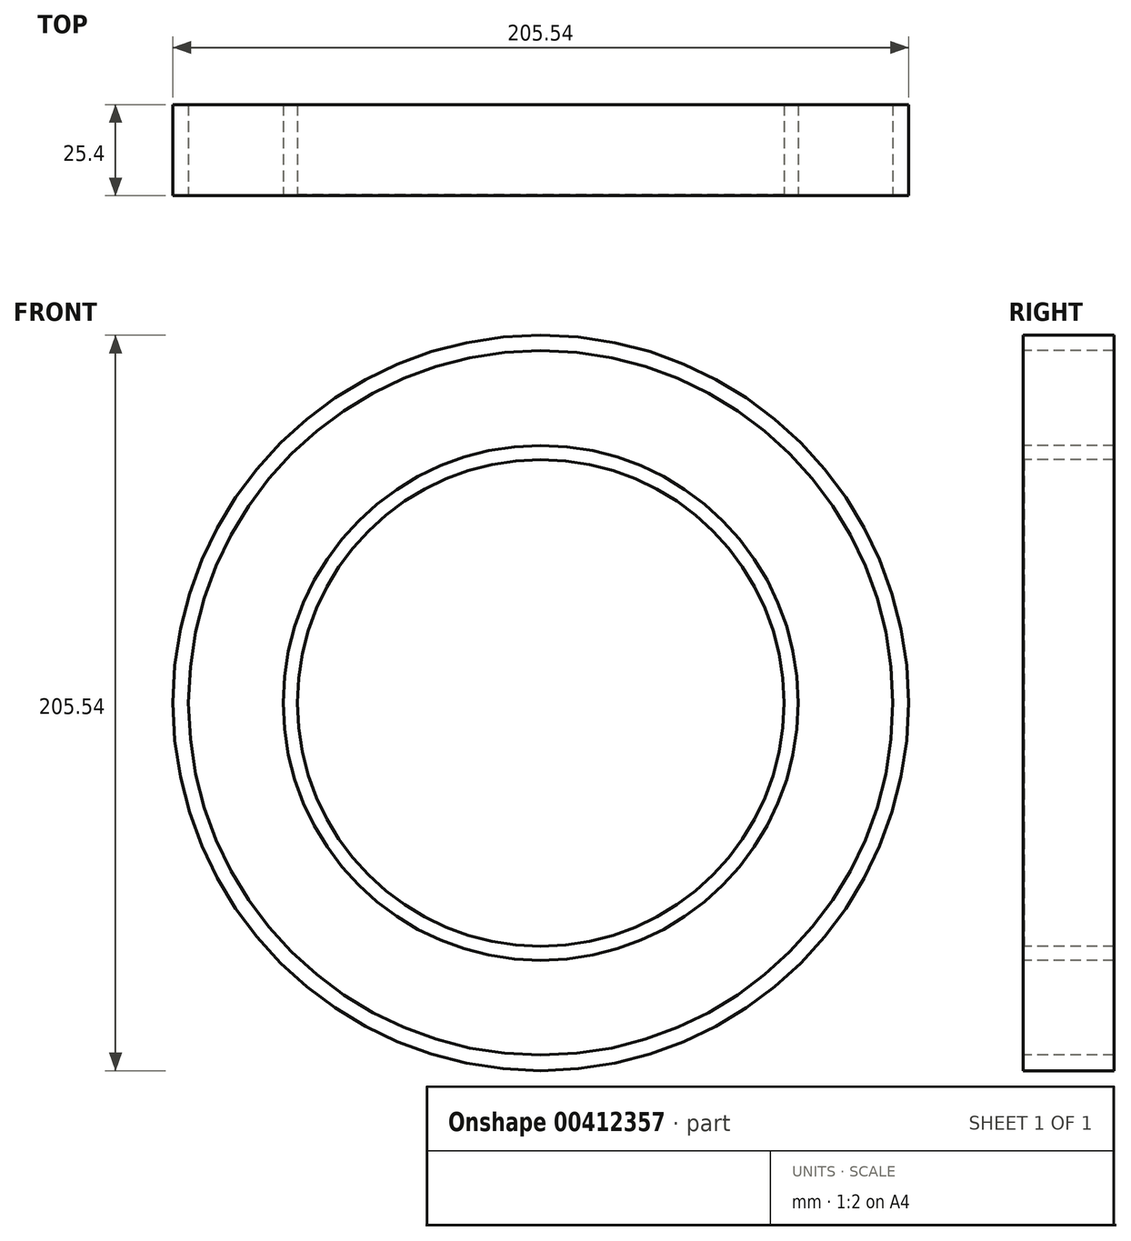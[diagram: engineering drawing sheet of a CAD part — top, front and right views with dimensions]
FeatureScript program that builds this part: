
annotation { "Feature Type Name" : "Feature", "Feature Type Description" : "" }
export const myFeature = defineFeature(function(context is Context, id is Id, definition is map)
    precondition{}
    {
        {
            var Q0;
            Q0=qCreatedBy(makeId("Front.planeOp"),FACE);
            var sketch = newSketch(context, id + "F0", { "sketchPlane" : qUnion([Q0])});
            skCircle(sketch, "E0", {"center": v(0, 0) * mm, "radius": 96.73 * mm});
            skCircle(sketch, "E1", {"center": v(0, 0) * mm, "radius": 101.89 * mm});
            skCircle(sketch, "E2", {"center": v(0, 0) * mm, "radius": 73.38 * mm});
            skCircle(sketch, "E3", {"center": v(0, 0) * mm, "radius": 68 * mm});
            skSolve(sketch);
        }
        {
            var Q0;
            Q0=makeQuery(id+"F0.imprint","IMPRINT",FACE,{"disambiguationData":[TD([[makeQuery(id+"F0.imprint","IMPRINT",EDGE,{"derivedFrom":sQuery(id+"F0.wireOp",EDGE,"E3")}),1.0]])]});
            var Q1;
            Q1=sQuery(id+"F0.wireOp",EDGE,"E3");
            extrude(context, id + "F1", {"entities" : qUnion([Q0]), "bodyType" : ToolBodyType.SURFACE, "surfaceEntities" : qUnion([Q1]), "depth" : 25.13 * mm});
        }
        {
            var Q0;
            Q0=qCreatedBy(makeId("Front.planeOp"),FACE);
            var sketch = newSketch(context, id + "F2", { "sketchPlane" : qUnion([Q0])});
            skCircle(sketch, "E4", {"center": v(0, 0) * mm, "radius": 71.95 * mm});
            skSolve(sketch);
        }
        {
            var Q0;
            Q0=makeQuery(id+"F2.imprint","IMPRINT",FACE,{"disambiguationData":[TD([[makeQuery(id+"F2.imprint","IMPRINT",EDGE,{"derivedFrom":sQuery(id+"F2.wireOp",EDGE,"E4")}),1.0]])]});
            var Q1;
            Q1=sQuery(id+"F2.wireOp",EDGE,"E4");
            extrude(context, id + "F3", {"entities" : qUnion([Q0]), "bodyType" : ToolBodyType.SURFACE, "surfaceEntities" : qUnion([Q1]), "depth" : 25.4 * mm});
        }
        {
            var Q0;
            Q0=qCreatedBy(makeId("Front.planeOp"),FACE);
            var sketch = newSketch(context, id + "F4", { "sketchPlane" : qUnion([Q0])});
            skCircle(sketch, "E5", {"center": v(0, 0) * mm, "radius": 98.42 * mm});
            skSolve(sketch);
        }
        {
            var Q0;
            Q0 = qSketchRegion(id + "F4", true);
            var Q1;
            Q1=sQuery(id+"F4.wireOp",EDGE,"E5");
            extrude(context, id + "F5", {"entities" : qUnion([Q0]), "bodyType" : ToolBodyType.SURFACE, "surfaceEntities" : qUnion([Q1]), "depth" : 25.4 * mm});
        }
        {
            var Q0;
            Q0=qCreatedBy(makeId("Front.planeOp"),FACE);
            var sketch = newSketch(context, id + "F6", { "sketchPlane" : qUnion([Q0])});
            skCircle(sketch, "E6", {"center": v(0, 0) * mm, "radius": 102.77 * mm});
            skSolve(sketch);
        }
        {
            var Q0;
            Q0 = qSketchRegion(id + "F6", true);
            var Q1;
            Q1=sQuery(id+"F6.wireOp",EDGE,"E6");
            extrude(context, id + "F7", {"entities" : qUnion([Q0]), "bodyType" : ToolBodyType.SURFACE, "surfaceEntities" : qUnion([Q1]), "depth" : 25.4 * mm});
        }
    });
